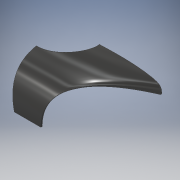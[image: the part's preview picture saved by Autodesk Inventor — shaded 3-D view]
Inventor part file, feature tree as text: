
AUTODESK INVENTOR PART (.ipt)
format: ipt  version: 2019 (Build 230136000, 136)  size: 1,319,424 bytes
history: native  units: mm
features: plane x27, sketch x24, extrude x11, fillet x6, mirror x5, loft x4, chamfer x3, other x1
ambient origin geometry x8: Origin, YZ Plane, XZ Plane, XY Plane, X Axis, Y Axis, Z Axis, Center Point
bodies: Body1 (feature_tree)
feature tree (81):
  sketch  "Sketch1"  dims[d2=55.0mm d5=-107.0mm d13=5.0mm d14=50.0mm]
  plane  "Work Plane1"
  sketch  "Sketch2"  dims[d15=70.0mm d16=5.0mm]
  sketch  "Sketch3"  dims[d17=0.0mm d18=90.0deg d19=0.0mm d20=90.0deg d21=0.0mm d22=90.0deg d23=2.0mm]
  plane  "Work Plane2"
  loft  "Loft2"
  mirror  "Mirror2"
  fillet  "Fillet1"  Radius=5.0mm
  fillet  "Fillet4"  Radius=50.0mm
  plane  "Work Plane3"
  plane  "Work Plane4"
  extrude  "Extrusion1"  Depth=5.0mm
  plane  "Work Plane5"
  extrude  "Extrusion2"  TaperAngle=0.0deg  [1 undecoded]
  fillet  "Fillet5"  [1 undecoded]
  mirror  "Mirror3"
  plane  "Work Plane22"
  plane  "Work Plane6"
  plane  "Work Plane7"
  fillet  "Fillet11"  Radius=2.0mm
  extrude  "Extrusion7"  Depth=87.5mm
  mirror  "Mirror4"
  plane  "Work Plane8"
  plane  "Work Plane9"
  sketch  "Sketch20"  dims[d42=2.0mm]
  plane  "Work Plane10"
  sketch  "Sketch21"  dims[d43=2.0mm]
  plane  "Work Plane11"
  sketch  "Sketch22"  dims[d44=2.0mm]
  loft  "Loft5"
  plane  "Work Plane13"
  sketch  "Sketch25"  dims[d45=2.0mm]
  plane  "Work Plane18"
  loft  "Loft6"
  mirror  "Mirror5"
  plane  "Work Plane19"
  extrude  "Extrusion9"  Depth=2.0mm
  fillet  "Fillet12"  Radius=2.0mm
  fillet  "Fillet14"  Radius=2.0mm
  plane  "Work Plane20"
  plane  "Work Plane21"
  plane  "Work Plane23"
  plane  "Work Plane24"
  plane  "Work Plane25"
  sketch  "Sketch33"  dims[d48=2.0mm]
  plane  "Work Plane26"
  sketch  "Sketch34"  dims[d49=2.0mm d50=2.0mm d51=1.0mm]
  plane  "Work Plane27"
  sketch  "Sketch35"  dims[d79=-25.0mm]
  plane  "Work Plane30"
  sketch  "Sketch38"  dims[d84=2.0mm]
  plane  "Work Plane31"
  plane  "Work Plane35"
  chamfer  "Chamfer7"  Distance=2.0mm
  chamfer  "Chamfer8"  Distance=28.0mm
  chamfer  "Chamfer9"  Distance=22.0mm
  loft  "Loft10"
  mirror  "Mirror9"
  plane  "Work Plane37"
  extrude  "Extrusion24"  Depth=70.0mm
  extrude  "Extrusion25"  Depth=10.0mm
  extrude  "Extrusion26"  Depth=10.0mm
  extrude  "Extrusion27"  TaperAngle=0.0deg  [1 undecoded]
  plane  "Work Plane38"
  extrude  "Extrusion28"  TaperAngle=0.0deg  [1 undecoded]
  extrude  "Extrusion29"  TaperAngle=0.0deg  [1 undecoded]
  extrude  "Extrusion30"  [1 undecoded]
  sketch  "Sketch4"  dims[d29=1.0mm d30=-4.5mm d31=87.5mm]
  sketch  "Sketch5"  dims[d32=0.0mm d33=0.0mm d34=-28.0mm]
  sketch  "Sketch6"  dims[d35=15.0mm d36=3.0mm]
  sketch  "Sketch17"  dims[d37=0.0mm d38=0.0mm d39=2.0mm d40=2.0mm d41=2.0mm]
  sketch  "Sketch27"  dims[d46=2.0mm]
  other  "Edges1"
  sketch  "Sketch28"  dims[d47=2.0mm]
  sketch  "Sketch47"  dims[d85=13.5mm]
  sketch  "Sketch48"  dims[d86=3.0mm]
  sketch  "Sketch49"  dims[d87=5.0mm]
  sketch  "Sketch50"  dims[d88=6.0mm d89=28.0mm d90=0.0mm d91=22.0mm d101=200.0mm]
  sketch  "Sketch51"  dims[d104=5.0mm d105=50.0mm d106=-80.0mm d107=45.0mm]
  sketch  "Sketch52"  dims[d108=3.0mm d109=70.0mm]
  sketch  "Sketch53"  dims[d110=80.0mm d111=3.0mm d112=20.0mm d123=0.0mm d124=90.0deg d125=0.0mm d126=90.0deg d127=0.0mm d128=90.0deg d129=-20.0mm d131=2.0mm d132=80.0mm d133=10.0mm d134=0.0mm d135=0.0mm d136=90.0deg d137=0.0mm d138=90.0deg d139=0.0mm d140=90.0deg d141=3.0mm d142=7.0mm d143=10.0mm d144=0.0mm d145=70.0mm d147=10.0mm d171=35.75mm d174=-8.25mm d177=20.0mm d179=30.0mm d180=5.0mm d181=41.5mm d182=15.0mm d183=10.0mm d184=5.0mm d200=-2.0mm d219=15.0mm d241=2.0mm d242=2.0mm d243=45.0deg d244=1.0mm d245=2.0mm d246=45.0deg d247=0.5mm d248=2.0mm d249=45.0deg d250=5.0mm d251=0.0mm d252=90.0deg d253=0.0mm d254=90.0deg d255=0.0mm d256=90.0deg d261=0.0mm d262=0.0mm d263=10.0mm d264=0.0mm d265=5.0mm d266=0.0mm d267=4.0mm d268=20.0mm d269=0.0mm d270=16.0mm d271=14.0mm d272=20.0mm d273=0.0mm d274=4.0mm d275=20.0mm d276=0.0mm d277=0.0mm d278=0.0mm]
note: 6 required parameter values undecoded (feature->parameter linkage not recoverable at this tier; creation-order binding heuristic only, values carry confidence <= 0.55)
